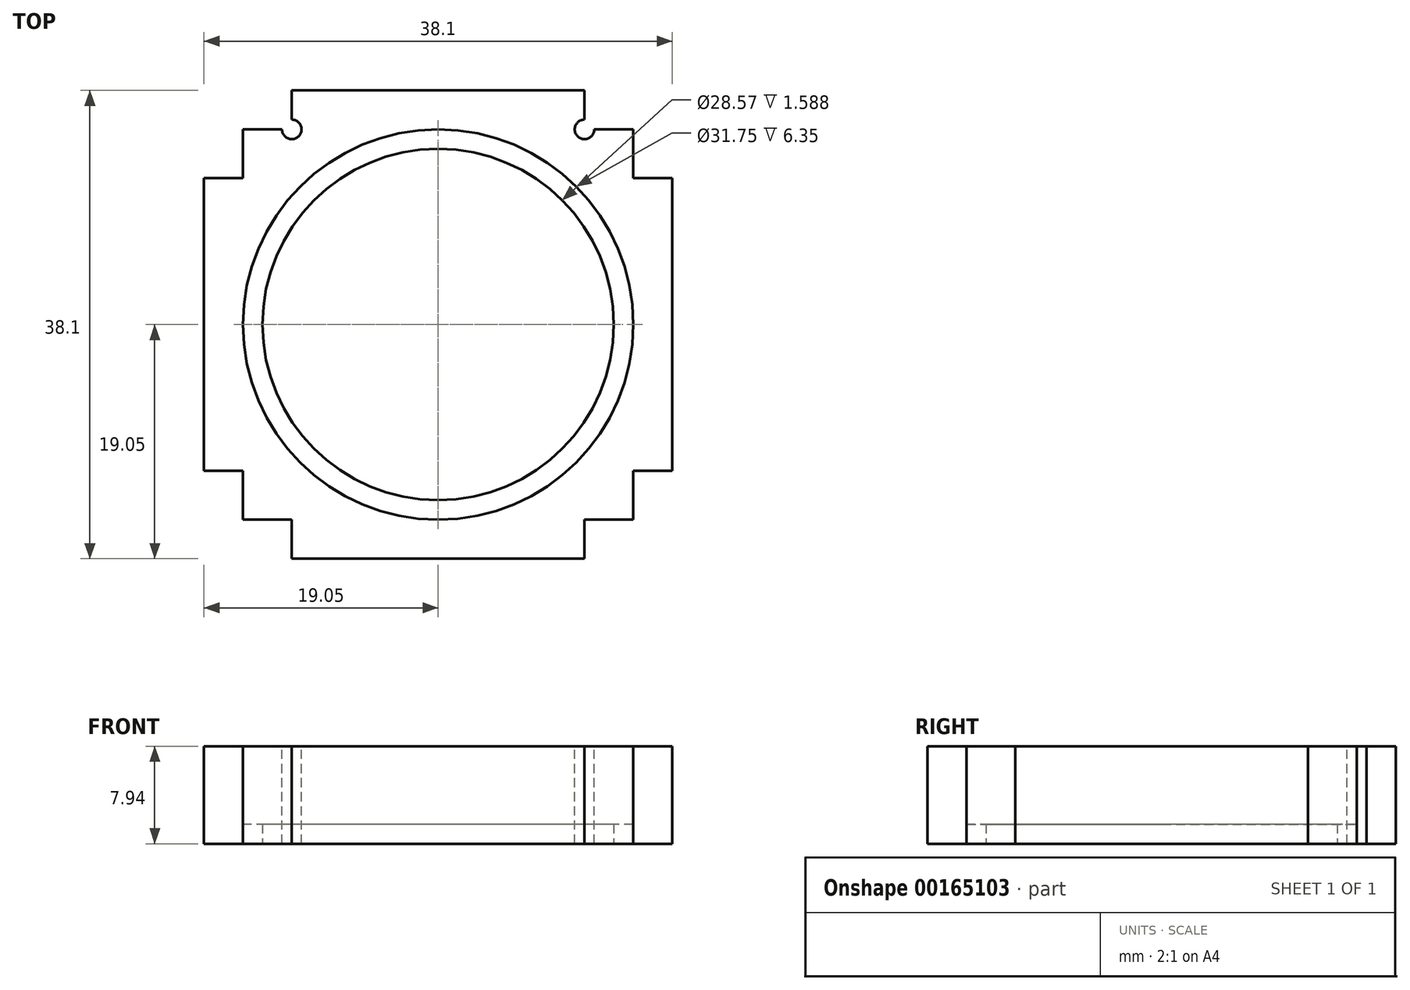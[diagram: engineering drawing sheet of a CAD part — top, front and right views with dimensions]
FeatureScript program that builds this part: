
annotation { "Feature Type Name" : "Feature", "Feature Type Description" : "" }
export const myFeature = defineFeature(function(context is Context, id is Id, definition is map)
    precondition{}
    {
        {
            var Q0;
            Q0=qCreatedBy(makeId("Top.planeOp"),FACE);
            var sketch = newSketch(context, id + "F0", { "sketchPlane" : qUnion([Q0])});
            skCircle(sketch, "E0", {"center": v(0, 0) * mm, "radius": 15.88 * mm, "construction": true});
            skLineSegment(sketch, "E1", {"start": v(0, 15.87) * mm, "end": v(0, -15.88) * mm, "construction": true});
            skLineSegment(sketch, "E2", {"start": v(-15.88, 0) * mm, "end": v(15.88, 0) * mm, "construction": true});
            skLineSegment(sketch, "E3.bottom", {"start": v(15.88, 11.9) * mm, "end": v(19.05, 11.9) * mm});
            skLineSegment(sketch, "E3.top", {"start": v(15.88, -11.9) * mm, "end": v(19.05, -11.9) * mm});
            skLineSegment(sketch, "E3.left", {"start": v(15.88, 11.9) * mm, "end": v(15.88, -11.9) * mm, "construction": true});
            skLineSegment(sketch, "E3.right", {"start": v(19.05, 11.9) * mm, "end": v(19.05, -11.9) * mm});
            skLineSegment(sketch, "E4", {"start": v(15.88, 11.9) * mm, "end": v(15.88, 15.87) * mm});
            skLineSegment(sketch, "E5", {"start": v(15.88, 15.88) * mm, "end": v(11.9, 15.88) * mm});
            skLineSegment(sketch, "E6.bottom", {"start": v(-11.9, 15.88) * mm, "end": v(11.9, 15.88) * mm, "construction": true});
            skLineSegment(sketch, "E6.top", {"start": v(-11.9, 19.05) * mm, "end": v(11.9, 19.05) * mm});
            skLineSegment(sketch, "E6.left", {"start": v(-11.9, 15.88) * mm, "end": v(-11.9, 19.05) * mm});
            skLineSegment(sketch, "E6.right", {"start": v(11.9, 15.88) * mm, "end": v(11.9, 19.05) * mm});
            skLineSegment(sketch, "E7.bottom", {"start": v(-15.88, 11.9) * mm, "end": v(-19.05, 11.9) * mm});
            skLineSegment(sketch, "E7.top", {"start": v(-15.88, -11.9) * mm, "end": v(-19.05, -11.9) * mm});
            skLineSegment(sketch, "E7.left", {"start": v(-15.88, 11.9) * mm, "end": v(-15.88, -11.9) * mm, "construction": true});
            skLineSegment(sketch, "E7.right", {"start": v(-19.05, 11.9) * mm, "end": v(-19.05, -11.9) * mm});
            skLineSegment(sketch, "E8.bottom", {"start": v(-11.9, -19.05) * mm, "end": v(11.9, -19.05) * mm});
            skLineSegment(sketch, "E8.top", {"start": v(-11.9, -15.88) * mm, "end": v(11.9, -15.88) * mm, "construction": true});
            skLineSegment(sketch, "E8.left", {"start": v(-11.9, -19.05) * mm, "end": v(-11.9, -15.88) * mm});
            skLineSegment(sketch, "E8.right", {"start": v(11.9, -19.05) * mm, "end": v(11.9, -15.87) * mm});
            skCircle(sketch, "E9", {"center": v(15.88, 11.9) * mm, "radius": 3.97 * mm, "construction": true});
            skLineSegment(sketch, "E10.bottom", {"start": v(-11.9, 15.88) * mm, "end": v(-15.88, 15.88) * mm});
            skLineSegment(sketch, "E10.right", {"start": v(-15.88, 15.87) * mm, "end": v(-15.88, 11.9) * mm});
            skLineSegment(sketch, "E11.top", {"start": v(-15.88, -15.88) * mm, "end": v(-11.9, -15.88) * mm});
            skLineSegment(sketch, "E11.left", {"start": v(-15.88, -11.9) * mm, "end": v(-15.88, -15.88) * mm});
            skLineSegment(sketch, "E12.bottom", {"start": v(11.9, -15.88) * mm, "end": v(15.88, -15.88) * mm});
            skLineSegment(sketch, "E12.right", {"start": v(15.88, -15.88) * mm, "end": v(15.88, -11.9) * mm});
            skCircle(sketch, "E13", {"center": v(0, 0) * mm, "radius": 14.29 * mm});
            skCircle(sketch, "E14", {"center": v(15.88, 11.9) * mm, "radius": 0.8 * mm, "construction": true});
            skSolve(sketch);
        }
        {
            var Q0;
            Q0 = qSketchRegion(id + "F0", true);
            extrude(context, id + "F1", {"entities" : qUnion([Q0]), "depth" : 7.94 * mm});
        }
        {
            var Q0;
            Q0=makeQuery(id+"F1.opExtrude","CAP_FACE",FACE,{"disambiguationData":[OSD([sQuery(id+"F0.wireOp",EDGE,"E3.bottom"),sQuery(id+"F0.wireOp",EDGE,"E3.top"),sQuery(id+"F0.wireOp",EDGE,"E3.right"),sQuery(id+"F0.wireOp",EDGE,"E4"),sQuery(id+"F0.wireOp",EDGE,"E5"),sQuery(id+"F0.wireOp",EDGE,"E6.top"),sQuery(id+"F0.wireOp",EDGE,"E6.left"),sQuery(id+"F0.wireOp",EDGE,"E6.right"),sQuery(id+"F0.wireOp",EDGE,"E7.bottom"),sQuery(id+"F0.wireOp",EDGE,"E7.top"),sQuery(id+"F0.wireOp",EDGE,"E7.right"),sQuery(id+"F0.wireOp",EDGE,"E8.bottom"),sQuery(id+"F0.wireOp",EDGE,"E8.left"),sQuery(id+"F0.wireOp",EDGE,"E8.right"),sQuery(id+"F0.wireOp",EDGE,"E10.bottom"),sQuery(id+"F0.wireOp",EDGE,"E10.right"),sQuery(id+"F0.wireOp",EDGE,"E11.top"),sQuery(id+"F0.wireOp",EDGE,"E11.left"),sQuery(id+"F0.wireOp",EDGE,"E12.bottom"),sQuery(id+"F0.wireOp",EDGE,"E12.right"),sQuery(id+"F0.wireOp",EDGE,"E13")])],"isStart":false});
            var sketch = newSketch(context, id + "F2", { "sketchPlane" : qUnion([Q0])});
            skCircle(sketch, "E15", {"center": v(0, 0) * mm, "radius": 15.88 * mm});
            skSolve(sketch);
        }
        {
            var Q0;
            Q0 = qSketchRegion(id + "F2", true);
            extrude(context, id + "F3", {"entities" : qUnion([Q0]), "operationType" : NewBodyOperationType.REMOVE, "oppositeDirection" : true, "depth" : 6.35 * mm});
        }
        {
            var Q0;
            Q0=makeQuery(id+"F1.opExtrude","CAP_FACE",FACE,{"disambiguationData":[OSD([sQuery(id+"F0.wireOp",EDGE,"E3.bottom"),sQuery(id+"F0.wireOp",EDGE,"E3.top"),sQuery(id+"F0.wireOp",EDGE,"E3.right"),sQuery(id+"F0.wireOp",EDGE,"E4"),sQuery(id+"F0.wireOp",EDGE,"E5"),sQuery(id+"F0.wireOp",EDGE,"E6.top"),sQuery(id+"F0.wireOp",EDGE,"E6.left"),sQuery(id+"F0.wireOp",EDGE,"E6.right"),sQuery(id+"F0.wireOp",EDGE,"E7.bottom"),sQuery(id+"F0.wireOp",EDGE,"E7.top"),sQuery(id+"F0.wireOp",EDGE,"E7.right"),sQuery(id+"F0.wireOp",EDGE,"E8.bottom"),sQuery(id+"F0.wireOp",EDGE,"E8.left"),sQuery(id+"F0.wireOp",EDGE,"E8.right"),sQuery(id+"F0.wireOp",EDGE,"E10.bottom"),sQuery(id+"F0.wireOp",EDGE,"E10.right"),sQuery(id+"F0.wireOp",EDGE,"E11.top"),sQuery(id+"F0.wireOp",EDGE,"E11.left"),sQuery(id+"F0.wireOp",EDGE,"E12.bottom"),sQuery(id+"F0.wireOp",EDGE,"E12.right"),sQuery(id+"F0.wireOp",EDGE,"E13")])],"isStart":false});
            var sketch = newSketch(context, id + "F4", { "sketchPlane" : qUnion([Q0])});
            skCircle(sketch, "E16", {"center": v(11.9, 15.88) * mm, "radius": 0.8 * mm});
            skCircle(sketch, "E17", {"center": v(-11.9, 15.88) * mm, "radius": 0.8 * mm});
            skSolve(sketch);
        }
        {
            var Q0;
            Q0 = qSketchRegion(id + "F4", true);
            var Q1;
            Q1=makeQuery(id+"F1.opExtrude","CAP_FACE",FACE,{"disambiguationData":[OSD([sQuery(id+"F0.wireOp",EDGE,"E3.bottom"),sQuery(id+"F0.wireOp",EDGE,"E3.top"),sQuery(id+"F0.wireOp",EDGE,"E3.right"),sQuery(id+"F0.wireOp",EDGE,"E4"),sQuery(id+"F0.wireOp",EDGE,"E5"),sQuery(id+"F0.wireOp",EDGE,"E6.top"),sQuery(id+"F0.wireOp",EDGE,"E6.left"),sQuery(id+"F0.wireOp",EDGE,"E6.right"),sQuery(id+"F0.wireOp",EDGE,"E7.bottom"),sQuery(id+"F0.wireOp",EDGE,"E7.top"),sQuery(id+"F0.wireOp",EDGE,"E7.right"),sQuery(id+"F0.wireOp",EDGE,"E8.bottom"),sQuery(id+"F0.wireOp",EDGE,"E8.left"),sQuery(id+"F0.wireOp",EDGE,"E8.right"),sQuery(id+"F0.wireOp",EDGE,"E10.bottom"),sQuery(id+"F0.wireOp",EDGE,"E10.right"),sQuery(id+"F0.wireOp",EDGE,"E11.top"),sQuery(id+"F0.wireOp",EDGE,"E11.left"),sQuery(id+"F0.wireOp",EDGE,"E12.bottom"),sQuery(id+"F0.wireOp",EDGE,"E12.right"),sQuery(id+"F0.wireOp",EDGE,"E13")])],"isStart":true});
            extrude(context, id + "F5", {"entities" : qUnion([Q0]), "operationType" : NewBodyOperationType.REMOVE, "endBound" : BoundingType.UP_TO_SURFACE, "oppositeDirection" : true, "endBoundEntityFace" : qUnion([Q1]), "depth" : 25.4 * mm});
        }
    });
